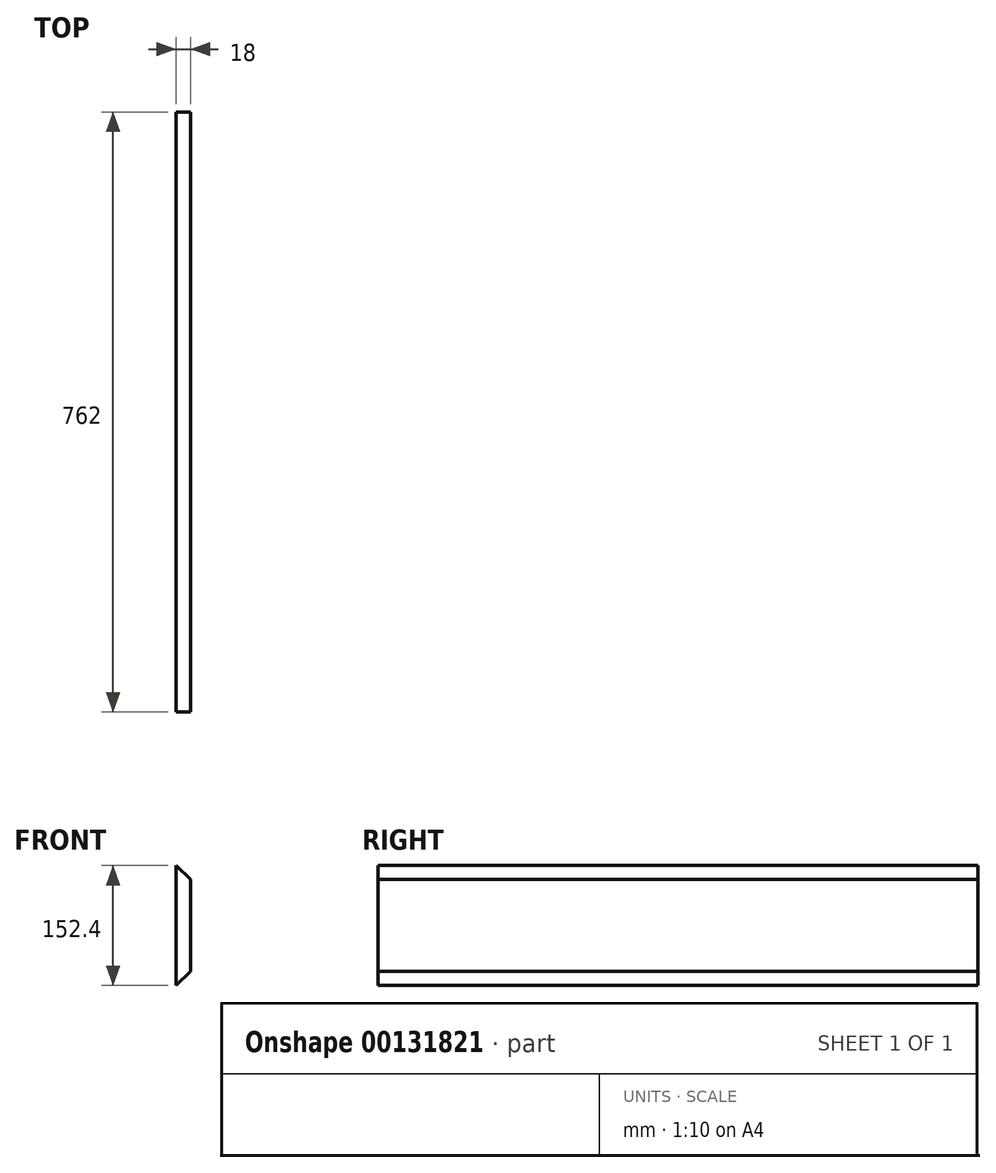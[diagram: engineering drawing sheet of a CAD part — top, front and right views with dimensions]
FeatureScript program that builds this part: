
annotation { "Feature Type Name" : "Feature", "Feature Type Description" : "" }
export const myFeature = defineFeature(function(context is Context, id is Id, definition is map)
    precondition{}
    {
        {
            var Q0;
            Q0=qCreatedBy(makeId("Right.planeOp"),FACE);
            var sketch = newSketch(context, id + "F0", { "sketchPlane" : qUnion([Q0])});
            skLineSegment(sketch, "E0.bottom", {"start": v(0, 0) * mm, "end": v(-762, 0) * mm});
            skLineSegment(sketch, "E0.top", {"start": v(0, 152.4) * mm, "end": v(-762, 152.4) * mm});
            skLineSegment(sketch, "E0.left", {"start": v(0, 0) * mm, "end": v(0, 152.4) * mm});
            skLineSegment(sketch, "E0.right", {"start": v(-762, 0) * mm, "end": v(-762, 152.4) * mm});
            skSolve(sketch);
        }
        {
            var Q0;
            Q0=makeQuery(id+"F0.imprint","IMPRINT",FACE,{"disambiguationData":[TD([[makeQuery(id+"F0.imprint","IMPRINT",EDGE,{"derivedFrom":sQuery(id+"F0.wireOp",EDGE,"E0.bottom")}),-1.0]])]});
            extrude(context, id + "F1", {"entities" : qUnion([Q0]), "depth" : 18 * mm});
        }
        {
            var Q0;
            Q0=makeQuery(id+"F1.opExtrude","CAP_EDGE",EDGE,{"disambiguationData":[OSD([sQuery(id+"F0.wireOp",EDGE,"E0.top")])],"isStart":false});
            var Q1;
            Q1=makeQuery(id+"F1.opExtrude","CAP_EDGE",EDGE,{"disambiguationData":[OSD([sQuery(id+"F0.wireOp",EDGE,"E0.bottom")])],"isStart":false});
            chamfer(context, id + "F2", {"entities" : qUnion([Q0, Q1]), "width" : 18 * mm, "tangentPropagation" : true});
        }
    });
